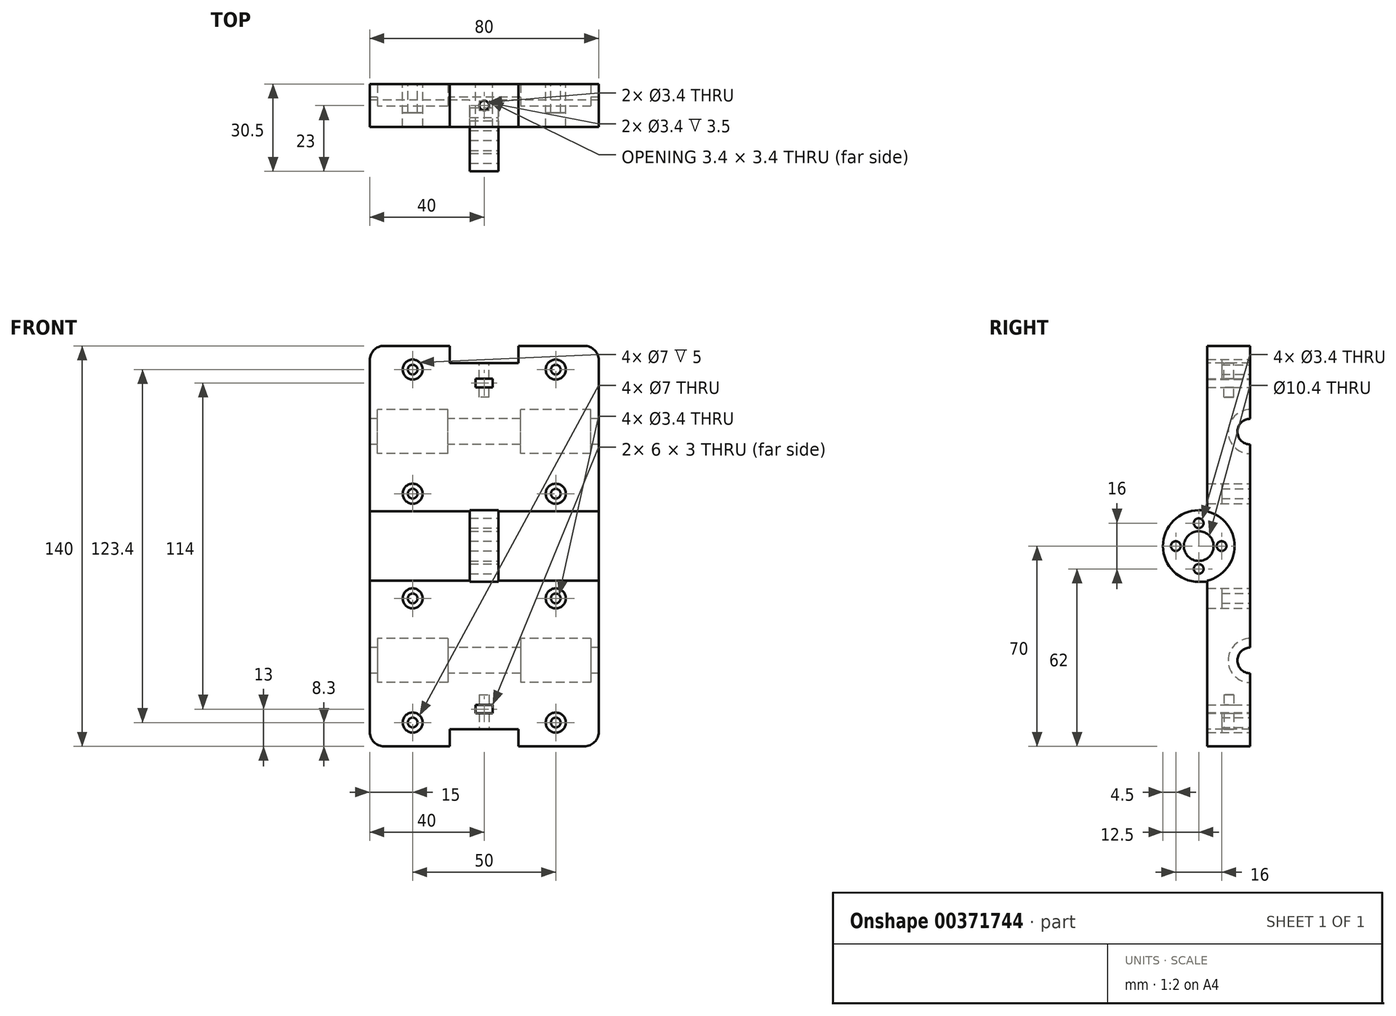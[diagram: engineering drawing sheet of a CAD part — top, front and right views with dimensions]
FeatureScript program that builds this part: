
annotation { "Feature Type Name" : "Feature", "Feature Type Description" : "" }
export const myFeature = defineFeature(function(context is Context, id is Id, definition is map)
    precondition{}
    {
        {
            var Q0;
            Q0=qCreatedBy(makeId("Front.planeOp"),FACE);
            var sketch = newSketch(context, id + "F0", { "sketchPlane" : qUnion([Q0])});
            skLineSegment(sketch, "E0.bottom", {"start": v(-35, 70) * mm, "end": v(35, 70) * mm});
            skLineSegment(sketch, "E0.top", {"start": v(-35, -70) * mm, "end": v(35, -70) * mm});
            skLineSegment(sketch, "E0.left", {"start": v(-40, 65) * mm, "end": v(-40, -65) * mm});
            skLineSegment(sketch, "E0.right", {"start": v(40, 65) * mm, "end": v(40, -65) * mm});
            skPoint(sketch, "E0.middle", {"position": v(0, 0) * mm});
            skPoint(sketch, "E1.visualSharp", {"position": v(-40, 70) * mm});
            skArc(sketch, "E1.filletArc", {"start": v(-35, 70) * mm, "mid": v(-38.54, 68.54) * mm, "end": v(-40, 65) * mm});
            skPoint(sketch, "E2.visualSharp", {"position": v(-40, -70) * mm});
            skArc(sketch, "E2.filletArc", {"start": v(-40, -65) * mm, "mid": v(-38.54, -68.54) * mm, "end": v(-35, -70) * mm});
            skPoint(sketch, "E3.visualSharp", {"position": v(40, -70) * mm});
            skArc(sketch, "E3.filletArc", {"start": v(35, -70) * mm, "mid": v(38.54, -68.54) * mm, "end": v(40, -65) * mm});
            skPoint(sketch, "E4.visualSharp", {"position": v(40, 70) * mm});
            skArc(sketch, "E4.filletArc", {"start": v(40, 65) * mm, "mid": v(38.54, 68.54) * mm, "end": v(35, 70) * mm});
            skLineSegment(sketch, "E5", {"start": v(0, 70) * mm, "end": v(0, 57) * mm, "construction": true});
            skLineSegment(sketch, "E6.bottom", {"start": v(-3, 58.5) * mm, "end": v(3, 58.5) * mm});
            skLineSegment(sketch, "E6.top", {"start": v(-3, 55.5) * mm, "end": v(3, 55.5) * mm});
            skLineSegment(sketch, "E6.left", {"start": v(-3, 58.5) * mm, "end": v(-3, 55.5) * mm});
            skLineSegment(sketch, "E6.right", {"start": v(3, 58.5) * mm, "end": v(3, 55.5) * mm});
            skPoint(sketch, "E6.middle", {"position": v(0, 57) * mm});
            skLineSegment(sketch, "E7", {"start": v(0, 0) * mm, "end": v(-40, 0) * mm, "construction": true});
            skLineSegment(sketch, "E8", {"start": v(0, -70) * mm, "end": v(0, -57) * mm, "construction": true});
            skLineSegment(sketch, "E9.bottom", {"start": v(-3, -55.5) * mm, "end": v(3, -55.5) * mm});
            skLineSegment(sketch, "E9.top", {"start": v(-3, -58.5) * mm, "end": v(3, -58.5) * mm});
            skLineSegment(sketch, "E9.left", {"start": v(-3, -55.5) * mm, "end": v(-3, -58.5) * mm});
            skLineSegment(sketch, "E9.right", {"start": v(3, -55.5) * mm, "end": v(3, -58.5) * mm});
            skPoint(sketch, "E9.middle", {"position": v(0, -57) * mm});
            skSolve(sketch);
        }
        {
            var Q0;
            Q0=makeQuery(id+"F0.imprint","IMPRINT",FACE,{"disambiguationData":[TD([[makeQuery(id+"F0.imprint","IMPRINT",EDGE,{"derivedFrom":sQuery(id+"F0.wireOp",EDGE,"E0.bottom")}),-1.0]])]});
            extrude(context, id + "F1", {"entities" : qUnion([Q0]), "depth" : 15 * mm});
        }
        {
            var Q0;
            Q0=makeQuery(id+"F1.opExtrude","CAP_FACE",FACE,{"disambiguationData":[OSD([sQuery(id+"F0.wireOp",EDGE,"E0.bottom"),sQuery(id+"F0.wireOp",EDGE,"E0.top"),sQuery(id+"F0.wireOp",EDGE,"E0.left"),sQuery(id+"F0.wireOp",EDGE,"E0.right"),sQuery(id+"F0.wireOp",EDGE,"rPnoFzad-uQuQ-coTz-bDe7-HXFcfHUqcX71"),sQuery(id+"F0.wireOp",EDGE,"TElXKnPJ-cZ4P-6HPu-AMil-aimtdiaow08g"),sQuery(id+"F0.wireOp",EDGE,"RZCtfZmF-zTxC-duFW-Uru4-HmVfb2UeuyBY"),sQuery(id+"F0.wireOp",EDGE,"BubEx5tJ-zZ3r-A3o4-4Zki-vEN1ARpqrYsd"),sQuery(id+"F0.wireOp",EDGE,"4ddce03b-fd9c-4e36-ac41-60a6f912cfc00.MirrorC"),sQuery(id+"F0.wireOp",EDGE,"63e85458-1495-4323-8014-057cedc1a4420.MirrorC"),sQuery(id+"F0.wireOp",EDGE,"1ce84351-db5b-4336-bf37-4880adbeb92d0.MirrorC"),sQuery(id+"F0.wireOp",EDGE,"cfc16f0e-f46d-4264-b5f4-874860700a590.MirrorC"),sQuery(id+"F0.wireOp",EDGE,"E1.filletArc"),sQuery(id+"F0.wireOp",EDGE,"E2.filletArc"),sQuery(id+"F0.wireOp",EDGE,"E3.filletArc"),sQuery(id+"F0.wireOp",EDGE,"E4.filletArc")])],"isStart":true});
            var sketch = newSketch(context, id + "F2", { "sketchPlane" : qUnion([Q0])});
            skLineSegment(sketch, "E10", {"start": v(0, 0) * mm, "end": v(0, 40) * mm, "construction": true});
            skLineSegment(sketch, "E11", {"start": v(0, 0) * mm, "end": v(0, -40) * mm, "construction": true});
            skCircle(sketch, "E12", {"center": v(0, 40) * mm, "radius": 7.7 * mm, "construction": true});
            skCircle(sketch, "E13", {"center": v(0, -40) * mm, "radius": 7.7 * mm, "construction": true});
            skLineSegment(sketch, "E14", {"start": v(0, 47.7) * mm, "end": v(-40, 47.7) * mm});
            skLineSegment(sketch, "E15", {"start": v(0, 47.7) * mm, "end": v(40, 47.7) * mm});
            skLineSegment(sketch, "E16", {"start": v(0, 32.3) * mm, "end": v(40, 32.3) * mm});
            skLineSegment(sketch, "E17", {"start": v(0, 32.3) * mm, "end": v(-40, 32.3) * mm});
            skLineSegment(sketch, "E18", {"start": v(-40, 47.7) * mm, "end": v(-40, 32.3) * mm});
            skLineSegment(sketch, "E19", {"start": v(40, 47.7) * mm, "end": v(40, 32.3) * mm});
            skLineSegment(sketch, "E20", {"start": v(0, -32.3) * mm, "end": v(-40, -32.3) * mm});
            skLineSegment(sketch, "E21", {"start": v(0, -47.7) * mm, "end": v(-40, -47.7) * mm});
            skLineSegment(sketch, "E22", {"start": v(0, -47.7) * mm, "end": v(40, -47.7) * mm});
            skLineSegment(sketch, "E23", {"start": v(0, -32.3) * mm, "end": v(40, -32.3) * mm});
            skLineSegment(sketch, "E24", {"start": v(-40, -32.3) * mm, "end": v(-40, -47.7) * mm});
            skLineSegment(sketch, "E25", {"start": v(40, -32.3) * mm, "end": v(40, -47.7) * mm});
            skLineSegment(sketch, "E26", {"start": v(25, 32.3) * mm, "end": v(12.7, 32.3) * mm});
            skLineSegment(sketch, "E27", {"start": v(25, 32.3) * mm, "end": v(37.3, 32.3) * mm});
            skLineSegment(sketch, "E28", {"start": v(12.7, 32.3) * mm, "end": v(25, 32.3) * mm, "construction": true});
            skLineSegment(sketch, "E29", {"start": v(25, 32.3) * mm, "end": v(37.3, 32.3) * mm, "construction": true});
            skLineSegment(sketch, "E30", {"start": v(12.7, 32.3) * mm, "end": v(12.7, 47.7) * mm});
            skLineSegment(sketch, "E31", {"start": v(37.3, 32.3) * mm, "end": v(37.3, 47.7) * mm});
            skLineSegment(sketch, "E32.MirrorCS", {"start": v(-12.7, 32.3) * mm, "end": v(-12.7, 47.7) * mm});
            skLineSegment(sketch, "E33.MirrorCS", {"start": v(-37.3, 32.3) * mm, "end": v(-37.3, 47.7) * mm});
            skLineSegment(sketch, "E34", {"start": v(0, 0) * mm, "end": v(18.6, 0) * mm, "construction": true});
            skLineSegment(sketch, "E35.MirrorCS", {"start": v(-37.3, -32.3) * mm, "end": v(-37.3, -47.7) * mm});
            skLineSegment(sketch, "E36.MirrorCS", {"start": v(-12.7, -32.3) * mm, "end": v(-12.7, -47.7) * mm});
            skLineSegment(sketch, "E37.MirrorCS", {"start": v(12.7, -32.3) * mm, "end": v(12.7, -47.7) * mm});
            skLineSegment(sketch, "E38.MirrorCS", {"start": v(37.3, -32.3) * mm, "end": v(37.3, -47.7) * mm});
            skLineSegment(sketch, "E39", {"start": v(25, 32.3) * mm, "end": v(25, 18.3) * mm, "construction": true});
            skLineSegment(sketch, "E40", {"start": v(25, 47.7) * mm, "end": v(25, 61.7) * mm, "construction": true});
            skCircle(sketch, "E41", {"center": v(25, 61.7) * mm, "radius": 1.7 * mm});
            skCircle(sketch, "E42", {"center": v(25, 18.3) * mm, "radius": 1.7 * mm});
            skCircle(sketch, "E43.MirrorC", {"center": v(-25, 61.7) * mm, "radius": 1.7 * mm});
            skCircle(sketch, "E44.MirrorC", {"center": v(-25, 18.3) * mm, "radius": 1.7 * mm});
            skCircle(sketch, "E45.MirrorC", {"center": v(25, -18.3) * mm, "radius": 1.7 * mm});
            skCircle(sketch, "E46.MirrorC", {"center": v(-25, -18.3) * mm, "radius": 1.7 * mm});
            skCircle(sketch, "E47.MirrorC", {"center": v(-25, -61.7) * mm, "radius": 1.7 * mm});
            skCircle(sketch, "E48.MirrorC", {"center": v(25, -61.7) * mm, "radius": 1.7 * mm});
            skCircle(sketch, "E49", {"center": v(-25, 61.7) * mm, "radius": 3.5 * mm});
            skCircle(sketch, "E50", {"center": v(-25, 18.3) * mm, "radius": 3.5 * mm});
            skCircle(sketch, "E51.MirrorC", {"center": v(25, 61.7) * mm, "radius": 3.5 * mm});
            skCircle(sketch, "E52.MirrorC", {"center": v(25, 18.3) * mm, "radius": 3.5 * mm});
            skCircle(sketch, "E53.MirrorC", {"center": v(-25, -18.3) * mm, "radius": 3.5 * mm});
            skCircle(sketch, "E54.MirrorC", {"center": v(-25, -61.7) * mm, "radius": 3.5 * mm});
            skCircle(sketch, "E55.MirrorC", {"center": v(25, -61.7) * mm, "radius": 3.5 * mm});
            skCircle(sketch, "E56.MirrorC", {"center": v(25, -18.3) * mm, "radius": 3.5 * mm});
            skSolve(sketch);
        }
        {
            var Q0;
            Q0=makeQuery(id+"F1.opExtrude","SWEPT_FACE",FACE,{"disambiguationData":[OSD([sQuery(id+"F0.wireOp",EDGE,"E0.left")])]});
            var sketch = newSketch(context, id + "F3", { "sketchPlane" : qUnion([Q0])});
            skLineSegment(sketch, "E57", {"start": v(0, 0) * mm, "end": v(0, 40) * mm, "construction": true});
            skLineSegment(sketch, "E58", {"start": v(0, 0) * mm, "end": v(0, -40) * mm, "construction": true});
            skCircle(sketch, "E59", {"center": v(0, 40) * mm, "radius": 7.7 * mm});
            skCircle(sketch, "E60", {"center": v(0, -40) * mm, "radius": 7.7 * mm});
            skCircle(sketch, "E61", {"center": v(0, 40) * mm, "radius": 4.5 * mm});
            skCircle(sketch, "E62", {"center": v(0, -40) * mm, "radius": 4.5 * mm});
            skSolve(sketch);
        }
        {
            var Q0;
            {var subQ0=sQuery(id+"F3.wireOp",EDGE,"E59");var subQ1=makeQuery(id+"F1.opExtrude","CAP_EDGE",EDGE,{"disambiguationData":[OSD([sQuery(id+"F0.wireOp",EDGE,"E0.left")])],"isStart":true});var subQ2=makeQuery(id+"F3.imprint","INTERSECT",VERTEX,{"disambiguationData":[OD(0.0)],"derivedFrom":[subQ1,subQ0]});Q0=makeQuery(id+"F3.imprint","IMPRINT",FACE,{"disambiguationData":[TD([[makeQuery(id+"F3.imprint","IMPRINT",EDGE,{"disambiguationData":[TD([[subQ2,1.0]])],"derivedFrom":subQ0}),1.0]])]});}
            var Q1;
            {var subQ0=sQuery(id+"F3.wireOp",EDGE,"E60");var subQ1=makeQuery(id+"F1.opExtrude","CAP_EDGE",EDGE,{"disambiguationData":[OSD([sQuery(id+"F0.wireOp",EDGE,"E0.left")])],"isStart":true});var subQ2=makeQuery(id+"F3.imprint","INTERSECT",VERTEX,{"disambiguationData":[OD(0.0)],"derivedFrom":[subQ1,subQ0]});Q1=makeQuery(id+"F3.imprint","IMPRINT",FACE,{"disambiguationData":[TD([[makeQuery(id+"F3.imprint","IMPRINT",EDGE,{"disambiguationData":[TD([[subQ2,-1.0]])],"derivedFrom":subQ0}),1.0]])]});}
            extrude(context, id + "F4", {"entities" : qUnion([Q0, Q1]), "operationType" : NewBodyOperationType.REMOVE, "oppositeDirection" : true, "depth" : 80 * mm});
        }
        {
            var Q0;
            {var subQ0=sQuery(id+"F2.wireOp",EDGE,"E18");Q0=makeQuery(id+"F2.imprint","IMPRINT",FACE,{"disambiguationData":[TD([[makeQuery(id+"F2.imprint","IMPRINT",EDGE,{"derivedFrom":subQ0}),1.0]])]});}
            var Q1;
            {var subQ3=sQuery(id+"F2.wireOp",EDGE,"E30");Q1=makeQuery(id+"F2.imprint","IMPRINT",FACE,{"disambiguationData":[TD([[makeQuery(id+"F2.imprint","IMPRINT",EDGE,{"derivedFrom":subQ3}),1.0]])]});}
            var Q2;
            {var subQ0=sQuery(id+"F2.wireOp",EDGE,"E19");Q2=makeQuery(id+"F2.imprint","IMPRINT",FACE,{"disambiguationData":[TD([[makeQuery(id+"F2.imprint","IMPRINT",EDGE,{"derivedFrom":subQ0}),-1.0]])]});}
            var Q3;
            {var subQ0=sQuery(id+"F2.wireOp",EDGE,"E24");Q3=makeQuery(id+"F2.imprint","IMPRINT",FACE,{"disambiguationData":[TD([[makeQuery(id+"F2.imprint","IMPRINT",EDGE,{"derivedFrom":subQ0}),1.0]])]});}
            var Q4;
            {var subQ7=sQuery(id+"F2.wireOp",EDGE,"E36.MirrorCS");Q4=makeQuery(id+"F2.imprint","IMPRINT",FACE,{"disambiguationData":[TD([[makeQuery(id+"F2.imprint","IMPRINT",EDGE,{"derivedFrom":subQ7}),1.0]])]});}
            var Q5;
            {var subQ0=sQuery(id+"F2.wireOp",EDGE,"E25");Q5=makeQuery(id+"F2.imprint","IMPRINT",FACE,{"disambiguationData":[TD([[makeQuery(id+"F2.imprint","IMPRINT",EDGE,{"derivedFrom":subQ0}),-1.0]])]});}
            extrude(context, id + "F5", {"entities" : qUnion([Q0, Q1, Q2, Q3, Q4, Q5]), "operationType" : NewBodyOperationType.ADD, "oppositeDirection" : true, "depth" : 10 * mm});
        }
        {
            var Q0;
            Q0=makeQuery(id+"F2.imprint","IMPRINT",FACE,{"disambiguationData":[TD([[makeQuery(id+"F2.imprint","IMPRINT",EDGE,{"derivedFrom":sQuery(id+"F2.wireOp",EDGE,"E43.MirrorC")}),-1.0]])]});
            var Q1;
            Q1=makeQuery(id+"F2.imprint","IMPRINT",FACE,{"disambiguationData":[TD([[makeQuery(id+"F2.imprint","IMPRINT",EDGE,{"derivedFrom":sQuery(id+"F2.wireOp",EDGE,"E41")}),1.0]])]});
            var Q2;
            Q2=makeQuery(id+"F2.imprint","IMPRINT",FACE,{"disambiguationData":[TD([[makeQuery(id+"F2.imprint","IMPRINT",EDGE,{"derivedFrom":sQuery(id+"F2.wireOp",EDGE,"E44.MirrorC")}),-1.0]])]});
            var Q3;
            Q3=makeQuery(id+"F2.imprint","IMPRINT",FACE,{"disambiguationData":[TD([[makeQuery(id+"F2.imprint","IMPRINT",EDGE,{"derivedFrom":sQuery(id+"F2.wireOp",EDGE,"E42")}),1.0]])]});
            var Q4;
            Q4=makeQuery(id+"F2.imprint","IMPRINT",FACE,{"disambiguationData":[TD([[makeQuery(id+"F2.imprint","IMPRINT",EDGE,{"derivedFrom":sQuery(id+"F2.wireOp",EDGE,"E46.MirrorC")}),1.0]])]});
            var Q5;
            Q5=makeQuery(id+"F2.imprint","IMPRINT",FACE,{"disambiguationData":[TD([[makeQuery(id+"F2.imprint","IMPRINT",EDGE,{"derivedFrom":sQuery(id+"F2.wireOp",EDGE,"E45.MirrorC")}),-1.0]])]});
            var Q6;
            Q6=makeQuery(id+"F2.imprint","IMPRINT",FACE,{"disambiguationData":[TD([[makeQuery(id+"F2.imprint","IMPRINT",EDGE,{"derivedFrom":sQuery(id+"F2.wireOp",EDGE,"E47.MirrorC")}),1.0]])]});
            var Q7;
            Q7=makeQuery(id+"F2.imprint","IMPRINT",FACE,{"disambiguationData":[TD([[makeQuery(id+"F2.imprint","IMPRINT",EDGE,{"derivedFrom":sQuery(id+"F2.wireOp",EDGE,"E48.MirrorC")}),-1.0]])]});
            extrude(context, id + "F6", {"entities" : qUnion([Q0, Q1, Q2, Q3, Q4, Q5, Q6, Q7]), "operationType" : NewBodyOperationType.REMOVE, "oppositeDirection" : true, "depth" : 25 * mm});
        }
        {
            var Q0;
            Q0=makeQuery(id+"F2.imprint","IMPRINT",FACE,{"disambiguationData":[TD([[makeQuery(id+"F2.imprint","IMPRINT",EDGE,{"derivedFrom":sQuery(id+"F2.wireOp",EDGE,"E43.MirrorC")}),1.0]])]});
            var Q1;
            Q1=makeQuery(id+"F2.imprint","IMPRINT",FACE,{"disambiguationData":[TD([[makeQuery(id+"F2.imprint","IMPRINT",EDGE,{"derivedFrom":sQuery(id+"F2.wireOp",EDGE,"E41")}),-1.0]])]});
            var Q2;
            Q2=makeQuery(id+"F2.imprint","IMPRINT",FACE,{"disambiguationData":[TD([[makeQuery(id+"F2.imprint","IMPRINT",EDGE,{"derivedFrom":sQuery(id+"F2.wireOp",EDGE,"E44.MirrorC")}),1.0]])]});
            var Q3;
            Q3=makeQuery(id+"F2.imprint","IMPRINT",FACE,{"disambiguationData":[TD([[makeQuery(id+"F2.imprint","IMPRINT",EDGE,{"derivedFrom":sQuery(id+"F2.wireOp",EDGE,"E42")}),-1.0]])]});
            var Q4;
            Q4=makeQuery(id+"F2.imprint","IMPRINT",FACE,{"disambiguationData":[TD([[makeQuery(id+"F2.imprint","IMPRINT",EDGE,{"derivedFrom":sQuery(id+"F2.wireOp",EDGE,"E46.MirrorC")}),-1.0]])]});
            var Q5;
            Q5=makeQuery(id+"F2.imprint","IMPRINT",FACE,{"disambiguationData":[TD([[makeQuery(id+"F2.imprint","IMPRINT",EDGE,{"derivedFrom":sQuery(id+"F2.wireOp",EDGE,"E45.MirrorC")}),1.0]])]});
            var Q6;
            Q6=makeQuery(id+"F2.imprint","IMPRINT",FACE,{"disambiguationData":[TD([[makeQuery(id+"F2.imprint","IMPRINT",EDGE,{"derivedFrom":sQuery(id+"F2.wireOp",EDGE,"E47.MirrorC")}),-1.0]])]});
            var Q7;
            Q7=makeQuery(id+"F2.imprint","IMPRINT",FACE,{"disambiguationData":[TD([[makeQuery(id+"F2.imprint","IMPRINT",EDGE,{"derivedFrom":sQuery(id+"F2.wireOp",EDGE,"E48.MirrorC")}),1.0]])]});
            extrude(context, id + "F7", {"entities" : qUnion([Q0, Q1, Q2, Q3, Q4, Q5, Q6, Q7]), "operationType" : NewBodyOperationType.REMOVE, "oppositeDirection" : true, "depth" : 25 * mm});
        }
        {
            var Q0;
            Q0=makeQuery(id+"F2.imprint","IMPRINT",FACE,{"disambiguationData":[TD([[makeQuery(id+"F2.imprint","IMPRINT",EDGE,{"derivedFrom":sQuery(id+"F2.wireOp",EDGE,"E43.MirrorC")}),1.0]])]});
            var Q1;
            Q1=makeQuery(id+"F2.imprint","IMPRINT",FACE,{"disambiguationData":[TD([[makeQuery(id+"F2.imprint","IMPRINT",EDGE,{"derivedFrom":sQuery(id+"F2.wireOp",EDGE,"E41")}),-1.0]])]});
            var Q2;
            Q2=makeQuery(id+"F2.imprint","IMPRINT",FACE,{"disambiguationData":[TD([[makeQuery(id+"F2.imprint","IMPRINT",EDGE,{"derivedFrom":sQuery(id+"F2.wireOp",EDGE,"E44.MirrorC")}),1.0]])]});
            var Q3;
            Q3=makeQuery(id+"F2.imprint","IMPRINT",FACE,{"disambiguationData":[TD([[makeQuery(id+"F2.imprint","IMPRINT",EDGE,{"derivedFrom":sQuery(id+"F2.wireOp",EDGE,"E42")}),-1.0]])]});
            var Q4;
            Q4=makeQuery(id+"F2.imprint","IMPRINT",FACE,{"disambiguationData":[TD([[makeQuery(id+"F2.imprint","IMPRINT",EDGE,{"derivedFrom":sQuery(id+"F2.wireOp",EDGE,"E46.MirrorC")}),-1.0]])]});
            var Q5;
            Q5=makeQuery(id+"F2.imprint","IMPRINT",FACE,{"disambiguationData":[TD([[makeQuery(id+"F2.imprint","IMPRINT",EDGE,{"derivedFrom":sQuery(id+"F2.wireOp",EDGE,"E45.MirrorC")}),1.0]])]});
            var Q6;
            Q6=makeQuery(id+"F2.imprint","IMPRINT",FACE,{"disambiguationData":[TD([[makeQuery(id+"F2.imprint","IMPRINT",EDGE,{"derivedFrom":sQuery(id+"F2.wireOp",EDGE,"E47.MirrorC")}),-1.0]])]});
            var Q7;
            Q7=makeQuery(id+"F2.imprint","IMPRINT",FACE,{"disambiguationData":[TD([[makeQuery(id+"F2.imprint","IMPRINT",EDGE,{"derivedFrom":sQuery(id+"F2.wireOp",EDGE,"E48.MirrorC")}),1.0]])]});
            extrude(context, id + "F8", {"entities" : qUnion([Q0, Q1, Q2, Q3, Q4, Q5, Q6, Q7]), "operationType" : NewBodyOperationType.ADD, "oppositeDirection" : true, "depth" : 10 * mm});
        }
        {
            var Q0;
            Q0=makeQuery(id+"F1.opExtrude","CAP_FACE",FACE,{"disambiguationData":[OSD([sQuery(id+"F0.wireOp",EDGE,"E0.bottom"),sQuery(id+"F0.wireOp",EDGE,"E0.top"),sQuery(id+"F0.wireOp",EDGE,"E0.left"),sQuery(id+"F0.wireOp",EDGE,"E0.right"),sQuery(id+"F0.wireOp",EDGE,"E1.filletArc"),sQuery(id+"F0.wireOp",EDGE,"E2.filletArc"),sQuery(id+"F0.wireOp",EDGE,"E3.filletArc"),sQuery(id+"F0.wireOp",EDGE,"E4.filletArc"),sQuery(id+"F0.wireOp",EDGE,"E6.bottom"),sQuery(id+"F0.wireOp",EDGE,"E6.top"),sQuery(id+"F0.wireOp",EDGE,"E6.left"),sQuery(id+"F0.wireOp",EDGE,"E6.right")])],"isStart":false});
            var sketch = newSketch(context, id + "F9", { "sketchPlane" : qUnion([Q0])});
            skLineSegment(sketch, "E63.bottom", {"start": v(-5, 12.5) * mm, "end": v(5, 12.5) * mm});
            skLineSegment(sketch, "E63.top", {"start": v(-5, -12.5) * mm, "end": v(5, -12.5) * mm});
            skLineSegment(sketch, "E63.left", {"start": v(-5, 12.5) * mm, "end": v(-5, -12.5) * mm});
            skLineSegment(sketch, "E63.right", {"start": v(5, 12.5) * mm, "end": v(5, -12.5) * mm});
            skPoint(sketch, "E63.middle", {"position": v(0, 0) * mm});
            skSolve(sketch);
        }
        {
            var Q0;
            Q0=makeQuery(id+"F9.imprint","IMPRINT",FACE,{"disambiguationData":[TD([[makeQuery(id+"F9.imprint","IMPRINT",EDGE,{"derivedFrom":sQuery(id+"F9.wireOp",EDGE,"E63.bottom")}),-1.0]])]});
            extrude(context, id + "F10", {"entities" : qUnion([Q0]), "operationType" : NewBodyOperationType.ADD, "depth" : 25 * mm});
        }
        {
            var Q0;
            Q0=makeQuery(id+"F10.opExtrude","SWEPT_FACE",FACE,{"disambiguationData":[OSD([sQuery(id+"F9.wireOp",EDGE,"E63.right")])]});
            var sketch = newSketch(context, id + "F11", { "sketchPlane" : qUnion([Q0])});
            skLineSegment(sketch, "E64", {"start": v(0, 0) * mm, "end": v(-18, 0) * mm, "construction": true});
            skPoint(sketch, "E64.endSnap0", {"position": v(-15, 0) * mm});
            skCircle(sketch, "E65", {"center": v(-18, 0) * mm, "radius": 5.2 * mm});
            skCircle(sketch, "E66", {"center": v(-18, 0) * mm, "radius": 8 * mm, "construction": true});
            skCircle(sketch, "E67", {"center": v(-18, 0) * mm, "radius": 12.5 * mm});
            skCircle(sketch, "E68", {"center": v(-18, 8) * mm, "radius": 1.7 * mm});
            skCircle(sketch, "E69", {"center": v(-26, 0) * mm, "radius": 1.7 * mm});
            skCircle(sketch, "E70", {"center": v(-18, -8) * mm, "radius": 1.7 * mm});
            skCircle(sketch, "E71", {"center": v(-10, 0) * mm, "radius": 1.7 * mm});
            skSolve(sketch);
        }
        {
            var Q0;
            Q0=makeQuery(id+"F1.opExtrude","SWEPT_FACE",FACE,{"disambiguationData":[OSD([sQuery(id+"F0.wireOp",EDGE,"E0.bottom")])]});
            var sketch = newSketch(context, id + "F12", { "sketchPlane" : qUnion([Q0])});
            skLineSegment(sketch, "E72", {"start": v(0, 0) * mm, "end": v(-12, 0) * mm});
            skLineSegment(sketch, "E73", {"start": v(0, 0) * mm, "end": v(12, 0) * mm});
            skLineSegment(sketch, "E74", {"start": v(-12, 0) * mm, "end": v(-12, -15) * mm});
            skLineSegment(sketch, "E75", {"start": v(12, 0) * mm, "end": v(12, -15) * mm});
            skLineSegment(sketch, "E76", {"start": v(12, -15) * mm, "end": v(-12, -15) * mm});
            skCircle(sketch, "E77", {"center": v(0, -7.5) * mm, "radius": 1.7 * mm});
            skPoint(sketch, "E77.centerSnap0", {"position": v(12, -7.5) * mm});
            skSolve(sketch);
        }
        {
            var Q0;
            {var subQ0=sQuery(id+"F11.wireOp",EDGE,"E65");var subQ1=makeQuery(id+"F10.opExtrude","CAP_EDGE",EDGE,{"disambiguationData":[OSD([sQuery(id+"F9.wireOp",EDGE,"E63.right")])],"isStart":true});var subQ2=makeQuery(id+"F11.imprint","INTERSECT",VERTEX,{"disambiguationData":[OD(0.0)],"derivedFrom":[subQ1,subQ0]});Q0=makeQuery(id+"F11.imprint","IMPRINT",FACE,{"disambiguationData":[TD([[makeQuery(id+"F11.imprint","IMPRINT",EDGE,{"disambiguationData":[TD([[subQ2,1.0]])],"derivedFrom":subQ0}),1.0]])]});}
            var Q1;
            {var subQ0=sQuery(id+"F11.wireOp",EDGE,"E65");var subQ1=makeQuery(id+"F10.opExtrude","CAP_EDGE",EDGE,{"disambiguationData":[OSD([sQuery(id+"F9.wireOp",EDGE,"E63.right")])],"isStart":true});var subQ2=makeQuery(id+"F11.imprint","INTERSECT",VERTEX,{"disambiguationData":[OD(0.0)],"derivedFrom":[subQ1,subQ0]});Q1=makeQuery(id+"F11.imprint","IMPRINT",FACE,{"disambiguationData":[TD([[makeQuery(id+"F11.imprint","IMPRINT",EDGE,{"disambiguationData":[TD([[subQ2,-1.0]])],"derivedFrom":subQ0}),1.0]])]});}
            var Q2;
            Q2=makeQuery(id+"F11.imprint","IMPRINT",FACE,{"disambiguationData":[TD([[makeQuery(id+"F11.imprint","IMPRINT",EDGE,{"derivedFrom":sQuery(id+"F11.wireOp",EDGE,"E68")}),1.0]])]});
            var Q3;
            Q3=makeQuery(id+"F11.imprint","IMPRINT",FACE,{"disambiguationData":[TD([[makeQuery(id+"F11.imprint","IMPRINT",EDGE,{"derivedFrom":sQuery(id+"F11.wireOp",EDGE,"E69")}),1.0]])]});
            var Q4;
            Q4=makeQuery(id+"F11.imprint","IMPRINT",FACE,{"disambiguationData":[TD([[makeQuery(id+"F11.imprint","IMPRINT",EDGE,{"derivedFrom":sQuery(id+"F11.wireOp",EDGE,"E70")}),1.0]])]});
            var Q5;
            Q5=makeQuery(id+"F11.imprint","IMPRINT",FACE,{"disambiguationData":[TD([[makeQuery(id+"F11.imprint","IMPRINT",EDGE,{"derivedFrom":sQuery(id+"F11.wireOp",EDGE,"E71")}),1.0]])]});
            var Q6;
            {var subQ1=sQuery(id+"F9.wireOp",EDGE,"E63.right");var subQ6=makeQuery(id+"F10.opExtrude","CAP_EDGE",EDGE,{"disambiguationData":[OSD([subQ1])],"isStart":false});Q6=makeQuery(id+"F11.imprint","IMPRINT",FACE,{"disambiguationData":[TD([[makeQuery(id+"F11.imprint","IMPRINT",EDGE,{"derivedFrom":subQ6}),1.0]])]});}
            extrude(context, id + "F13", {"entities" : qUnion([Q0, Q1, Q2, Q3, Q4, Q5, Q6]), "operationType" : NewBodyOperationType.REMOVE, "endBound" : BoundingType.SYMMETRIC, "oppositeDirection" : true, "depth" : 100 * mm});
        }
        {
            var Q0;
            Q0=makeQuery(id+"F11.imprint","IMPRINT",FACE,{"disambiguationData":[TD([[makeQuery(id+"F11.imprint","IMPRINT",EDGE,{"derivedFrom":sQuery(id+"F11.wireOp",EDGE,"E68")}),-1.0]])]});
            var Q1;
            Q1=makeQuery(id+"F11.imprint","IMPRINT",FACE,{"disambiguationData":[TD([[makeQuery(id+"F11.imprint","IMPRINT",EDGE,{"derivedFrom":sQuery(id+"F11.wireOp",EDGE,"E71")}),-1.0]])]});
            extrude(context, id + "F14", {"entities" : qUnion([Q0, Q1]), "operationType" : NewBodyOperationType.REMOVE, "endBound" : BoundingType.SYMMETRIC, "oppositeDirection" : true, "depth" : 100 * mm});
        }
        {
            var Q0;
            Q0=makeQuery(id+"F12.imprint","IMPRINT",FACE,{"disambiguationData":[TD([[makeQuery(id+"F12.imprint","IMPRINT",EDGE,{"derivedFrom":sQuery(id+"F12.wireOp",EDGE,"E72")}),-1.0]])]});
            extrude(context, id + "F15", {"entities" : qUnion([Q0]), "operationType" : NewBodyOperationType.REMOVE, "oppositeDirection" : true, "depth" : 6 * mm});
        }
        {
            var Q0;
            Q0=makeQuery(id+"F11.imprint","IMPRINT",FACE,{"disambiguationData":[TD([[makeQuery(id+"F11.imprint","IMPRINT",EDGE,{"derivedFrom":sQuery(id+"F11.wireOp",EDGE,"E68")}),-1.0]])]});
            var Q1;
            Q1=makeQuery(id+"F11.imprint","IMPRINT",FACE,{"disambiguationData":[TD([[makeQuery(id+"F11.imprint","IMPRINT",EDGE,{"derivedFrom":sQuery(id+"F11.wireOp",EDGE,"E71")}),-1.0]])]});
            extrude(context, id + "F16", {"entities" : qUnion([Q0, Q1]), "operationType" : NewBodyOperationType.ADD, "oppositeDirection" : true, "depth" : 10 * mm});
        }
        {
            var Q0;
            Q0=makeQuery(id+"F12.imprint","IMPRINT",FACE,{"disambiguationData":[TD([[makeQuery(id+"F12.imprint","IMPRINT",EDGE,{"derivedFrom":sQuery(id+"F12.wireOp",EDGE,"E77")}),1.0]])]});
            extrude(context, id + "F17", {"entities" : qUnion([Q0]), "operationType" : NewBodyOperationType.REMOVE, "oppositeDirection" : true, "depth" : 18 * mm});
        }
        {
            var Q0;
            Q0=makeQuery(id+"F1.opExtrude","SWEPT_FACE",FACE,{"disambiguationData":[OSD([sQuery(id+"F0.wireOp",EDGE,"E0.top")])]});
            var sketch = newSketch(context, id + "F18", { "sketchPlane" : qUnion([Q0])});
            skLineSegment(sketch, "E78", {"start": v(0, 0) * mm, "end": v(-12, 0) * mm});
            skLineSegment(sketch, "E79", {"start": v(0, 0) * mm, "end": v(12, 0) * mm});
            skLineSegment(sketch, "E80", {"start": v(12, 0) * mm, "end": v(12, 15) * mm});
            skLineSegment(sketch, "E81", {"start": v(-12, 0) * mm, "end": v(-12, 15) * mm});
            skLineSegment(sketch, "E82", {"start": v(-12, 15) * mm, "end": v(12, 15) * mm});
            skCircle(sketch, "E83", {"center": v(0, 7.5) * mm, "radius": 1.7 * mm});
            skPoint(sketch, "E83.centerSnap0", {"position": v(12, 7.5) * mm});
            skPoint(sketch, "E83.centerSnap1", {"position": v(0, 15) * mm});
            skSolve(sketch);
        }
        {
            var Q0;
            Q0=makeQuery(id+"F18.imprint","IMPRINT",FACE,{"disambiguationData":[TD([[makeQuery(id+"F18.imprint","IMPRINT",EDGE,{"derivedFrom":sQuery(id+"F18.wireOp",EDGE,"E78")}),1.0]])]});
            extrude(context, id + "F19", {"entities" : qUnion([Q0]), "operationType" : NewBodyOperationType.REMOVE, "oppositeDirection" : true, "depth" : 6 * mm});
        }
        {
            var Q0;
            Q0=makeQuery(id+"F0.imprint","IMPRINT",FACE,{"disambiguationData":[TD([[makeQuery(id+"F0.imprint","IMPRINT",EDGE,{"derivedFrom":sQuery(id+"F0.wireOp",EDGE,"E9.bottom")}),-1.0]])]});
            extrude(context, id + "F20", {"entities" : qUnion([Q0]), "operationType" : NewBodyOperationType.REMOVE, "oppositeDirection" : true, "depth" : 25 * mm});
        }
        {
            var Q0;
            Q0=makeQuery(id+"F18.imprint","IMPRINT",FACE,{"disambiguationData":[TD([[makeQuery(id+"F18.imprint","IMPRINT",EDGE,{"derivedFrom":sQuery(id+"F18.wireOp",EDGE,"E83")}),1.0]])]});
            extrude(context, id + "F21", {"entities" : qUnion([Q0]), "operationType" : NewBodyOperationType.REMOVE, "oppositeDirection" : true, "depth" : 18 * mm});
        }
        {
            var Q0;
            {var subQ0=sQuery(id+"F3.wireOp",EDGE,"E62");var subQ1=makeQuery(id+"F1.opExtrude","CAP_EDGE",EDGE,{"disambiguationData":[OSD([sQuery(id+"F0.wireOp",EDGE,"E0.left")])],"isStart":true});var subQ2=makeQuery(id+"F3.imprint","INTERSECT",VERTEX,{"disambiguationData":[OD(0.0)],"derivedFrom":[subQ1,subQ0]});Q0=makeQuery(id+"F3.imprint","IMPRINT",FACE,{"disambiguationData":[TD([[makeQuery(id+"F3.imprint","IMPRINT",EDGE,{"disambiguationData":[TD([[subQ2,1.0]])],"derivedFrom":subQ0}),1.0]])]});}
            var Q1;
            {var subQ0=sQuery(id+"F3.wireOp",EDGE,"E62");var subQ1=makeQuery(id+"F1.opExtrude","CAP_EDGE",EDGE,{"disambiguationData":[OSD([sQuery(id+"F0.wireOp",EDGE,"E0.left")])],"isStart":true});var subQ2=makeQuery(id+"F3.imprint","INTERSECT",VERTEX,{"disambiguationData":[OD(0.0)],"derivedFrom":[subQ1,subQ0]});Q1=makeQuery(id+"F3.imprint","IMPRINT",FACE,{"disambiguationData":[TD([[makeQuery(id+"F3.imprint","IMPRINT",EDGE,{"disambiguationData":[TD([[subQ2,-1.0]])],"derivedFrom":subQ0}),1.0]])]});}
            var Q2;
            {var subQ0=sQuery(id+"F3.wireOp",EDGE,"E61");var subQ1=makeQuery(id+"F1.opExtrude","CAP_EDGE",EDGE,{"disambiguationData":[OSD([sQuery(id+"F0.wireOp",EDGE,"E0.left")])],"isStart":true});var subQ2=makeQuery(id+"F3.imprint","INTERSECT",VERTEX,{"disambiguationData":[OD(0.0)],"derivedFrom":[subQ1,subQ0]});Q2=makeQuery(id+"F3.imprint","IMPRINT",FACE,{"disambiguationData":[TD([[makeQuery(id+"F3.imprint","IMPRINT",EDGE,{"disambiguationData":[TD([[subQ2,-1.0]])],"derivedFrom":subQ0}),1.0]])]});}
            var Q3;
            {var subQ0=sQuery(id+"F3.wireOp",EDGE,"E61");var subQ1=makeQuery(id+"F1.opExtrude","CAP_EDGE",EDGE,{"disambiguationData":[OSD([sQuery(id+"F0.wireOp",EDGE,"E0.left")])],"isStart":true});var subQ2=makeQuery(id+"F3.imprint","INTERSECT",VERTEX,{"disambiguationData":[OD(0.0)],"derivedFrom":[subQ1,subQ0]});Q3=makeQuery(id+"F3.imprint","IMPRINT",FACE,{"disambiguationData":[TD([[makeQuery(id+"F3.imprint","IMPRINT",EDGE,{"disambiguationData":[TD([[subQ2,1.0]])],"derivedFrom":subQ0}),1.0]])]});}
            extrude(context, id + "F22", {"entities" : qUnion([Q0, Q1, Q2, Q3]), "operationType" : NewBodyOperationType.REMOVE, "oppositeDirection" : true, "depth" : 80 * mm});
        }
    });
